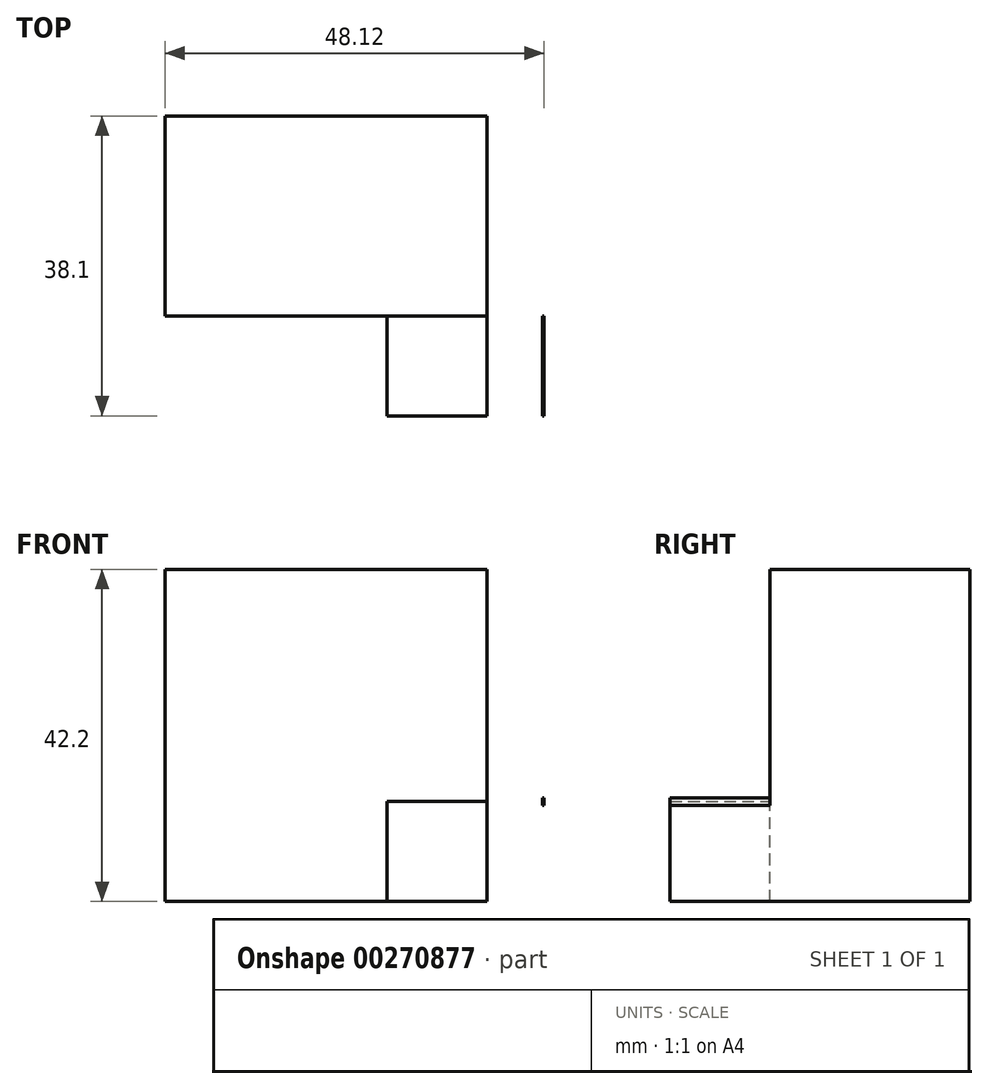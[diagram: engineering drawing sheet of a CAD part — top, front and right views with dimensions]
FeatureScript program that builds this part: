
annotation { "Feature Type Name" : "Feature", "Feature Type Description" : "" }
export const myFeature = defineFeature(function(context is Context, id is Id, definition is map)
    precondition{}
    {
        {
            var Q0;
            Q0=qCreatedBy(makeId("Front.planeOp"),FACE);
            var sketch = newSketch(context, id + "F0", { "sketchPlane" : qUnion([Q0])});
            skLineSegment(sketch, "E0.bottom", {"start": v(-42.58, 0) * mm, "end": v(-42.77, 0) * mm});
            skLineSegment(sketch, "E0.top", {"start": v(-42.58, 42.2) * mm, "end": v(-42.77, 42.2) * mm});
            skLineSegment(sketch, "E0.left", {"start": v(-42.58, 0) * mm, "end": v(-42.58, 42.2) * mm});
            skLineSegment(sketch, "E0.right", {"start": v(-42.77, 0) * mm, "end": v(-42.77, 42.2) * mm});
            skLineSegment(sketch, "E1.bottom", {"start": v(-1.9, 42.2) * mm, "end": v(-42.58, 42.2) * mm});
            skLineSegment(sketch, "E1.top", {"start": v(-1.9, 42.2) * mm, "end": v(-42.58, 42.2) * mm});
            skLineSegment(sketch, "E1.left", {"start": v(-1.9, 42.2) * mm, "end": v(-1.9, 42.2) * mm});
            skLineSegment(sketch, "E1.right", {"start": v(-42.58, 42.2) * mm, "end": v(-42.58, 42.2) * mm});
            skLineSegment(sketch, "E2.top", {"start": v(-1.9, 0) * mm, "end": v(-1.9, 0) * mm});
            skLineSegment(sketch, "E2.left", {"start": v(-1.9, 42.2) * mm, "end": v(-1.9, 0) * mm});
            skLineSegment(sketch, "E2.right", {"start": v(-1.9, 42.2) * mm, "end": v(-1.9, 0) * mm});
            skLineSegment(sketch, "E3.bottom", {"start": v(-42.58, 0) * mm, "end": v(-1.9, 0) * mm});
            skLineSegment(sketch, "E3.top", {"start": v(-42.58, 0) * mm, "end": v(-1.9, 0) * mm});
            skLineSegment(sketch, "E3.left", {"start": v(-42.58, 0) * mm, "end": v(-42.58, 0) * mm});
            skSolve(sketch);
        }
        {
            var Q0;
            Q0 = qSketchRegion(id + "F0", true);
            extrude(context, id + "F1", {"entities" : qUnion([Q0]), "depth" : 25.4 * mm});
        }
        {
            var Q0;
            Q0=makeQuery(id+"F1.opExtrude","CAP_FACE",FACE,{"disambiguationData":[OSD([sQuery(id+"F0.wireOp",EDGE,"E0.bottom"),sQuery(id+"F0.wireOp",EDGE,"E0.top"),sQuery(id+"F0.wireOp",EDGE,"E0.right"),sQuery(id+"F0.wireOp",EDGE,"E1.top"),sQuery(id+"F0.wireOp",EDGE,"E2.right"),sQuery(id+"F0.wireOp",EDGE,"E3.top")])],"isStart":false});
            var sketch = newSketch(context, id + "F2", { "sketchPlane" : qUnion([Q0])});
            skLineSegment(sketch, "E4.bottom", {"start": v(-1.9, 0) * mm, "end": v(-14.6, 0) * mm});
            skLineSegment(sketch, "E4.top", {"start": v(-1.9, 12.7) * mm, "end": v(-14.6, 12.7) * mm});
            skLineSegment(sketch, "E4.left", {"start": v(-1.9, 0) * mm, "end": v(-1.9, 12.7) * mm});
            skLineSegment(sketch, "E4.right", {"start": v(-14.6, 0) * mm, "end": v(-14.6, 12.7) * mm});
            skLineSegment(sketch, "E5.bottom", {"start": v(5.35, 13.18) * mm, "end": v(5.16, 13.18) * mm});
            skLineSegment(sketch, "E5.top", {"start": v(5.35, 12.22) * mm, "end": v(5.16, 12.22) * mm});
            skLineSegment(sketch, "E5.left", {"start": v(5.35, 13.18) * mm, "end": v(5.35, 12.22) * mm});
            skLineSegment(sketch, "E5.right", {"start": v(5.16, 13.18) * mm, "end": v(5.16, 12.22) * mm});
            skSolve(sketch);
        }
        {
            var Q0;
            Q0 = qSketchRegion(id + "F2", true);
            extrude(context, id + "F3", {"entities" : qUnion([Q0]), "operationType" : NewBodyOperationType.ADD, "depth" : 12.7 * mm});
        }
    });
